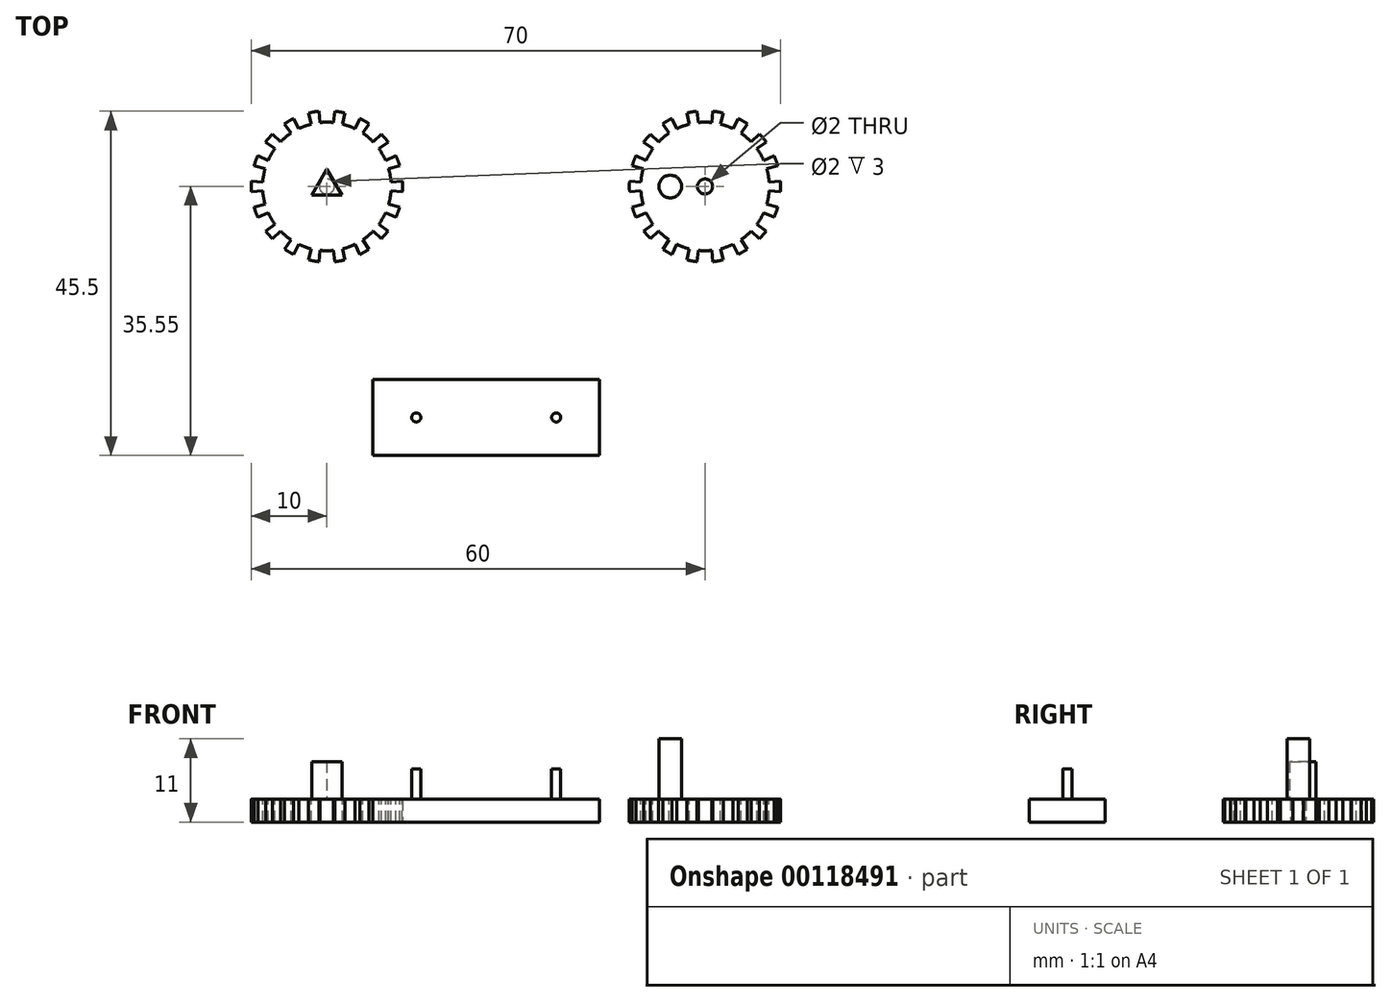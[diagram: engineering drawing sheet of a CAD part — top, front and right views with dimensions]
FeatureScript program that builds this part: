
annotation { "Feature Type Name" : "Feature", "Feature Type Description" : "" }
export const myFeature = defineFeature(function(context is Context, id is Id, definition is map)
    precondition{}
    {
        {
            var Q0;
            Q0=qCreatedBy(makeId("Top.planeOp"),FACE);
            var sketch = newSketch(context, id + "F0", { "sketchPlane" : qUnion([Q0])});
            skCircle(sketch, "E0", {"center": v(0, 0) * mm, "radius": 10 * mm});
            skSolve(sketch);
        }
        {
            var Q0;
            Q0=makeQuery(id+"F0.imprint","IMPRINT",FACE,{"disambiguationData":[TD([[makeQuery(id+"F0.imprint","IMPRINT",EDGE,{"derivedFrom":sQuery(id+"F0.wireOp",EDGE,"E0")}),1.0]])]});
            extrude(context, id + "F1", {"entities" : qUnion([Q0]), "depth" : 3 * mm});
        }
        {
            var Q0;
            Q0=makeQuery(id+"F1.opExtrude","CAP_FACE",FACE,{"disambiguationData":[OSD([sQuery(id+"F0.wireOp",EDGE,"E0")])],"isStart":false});
            var sketch = newSketch(context, id + "F2", { "sketchPlane" : qUnion([Q0])});
            skLineSegment(sketch, "E1", {"start": v(0, 10) * mm, "end": v(0, 8.5) * mm, "construction": true});
            skLineSegment(sketch, "E2", {"start": v(0.89, 8.45) * mm, "end": v(1.05, 9.95) * mm});
            skArc(sketch, "E3", {"start": v(0.89, 8.45) * mm, "mid": v(0, 8.5) * mm, "end": v(-0.89, 8.45) * mm});
            skLineSegment(sketch, "E4.MirrorCS", {"start": v(-0.89, 8.45) * mm, "end": v(-1.05, 9.95) * mm});
            skArc(sketch, "E5.0", {"start": v(1.05, 9.95) * mm, "mid": v(0, 10) * mm, "end": v(-1.05, 9.95) * mm});
            skSolve(sketch);
        }
        {
            var Q0;
            Q0=makeQuery(id+"F2.imprint","IMPRINT",FACE,{"disambiguationData":[TD([[makeQuery(id+"F2.imprint","IMPRINT",EDGE,{"derivedFrom":sQuery(id+"F2.wireOp",EDGE,"E2")}),1.0]])]});
            extrude(context, id + "F3", {"entities" : qUnion([Q0]), "operationType" : NewBodyOperationType.REMOVE, "endBound" : BoundingType.THROUGH_ALL, "oppositeDirection" : true, "depth" : 25 * mm});
        }
        {
            var Q0;
            Q0=makeQuery(id+"F1.opExtrude","SWEPT_BODY",BODY,{"disambiguationData":[OSD([sQuery(id+"F0.wireOp",EDGE,"E0")])]});
            var Q1;
            Q1=makeQuery(id+"F3.boolean.opBoolean","COPY",FACE,{"derivedFrom":makeQuery(id+"F3.opExtrude","SWEPT_FACE",FACE,{"disambiguationData":[OSD([sQuery(id+"F2.wireOp",EDGE,"E4.MirrorCS")])]})});
            var Q2;
            Q2=makeQuery(id+"F3.boolean.opBoolean","COPY",FACE,{"derivedFrom":makeQuery(id+"F3.opExtrude","SWEPT_FACE",FACE,{"disambiguationData":[OSD([sQuery(id+"F2.wireOp",EDGE,"E3")])]})});
            var Q3;
            Q3=makeQuery(id+"F3.boolean.opBoolean","COPY",FACE,{"derivedFrom":makeQuery(id+"F3.opExtrude","SWEPT_FACE",FACE,{"disambiguationData":[OSD([sQuery(id+"F2.wireOp",EDGE,"E2")])]})});
            var Q4;
            Q4=makeQuery(id+"F1.opExtrude","SWEPT_FACE",FACE,{"disambiguationData":[OSD([sQuery(id+"F0.wireOp",EDGE,"E0")])]});
            circularPattern(context, id + "F4", {"patternType" : PatternType.FACE, "faces" : qUnion([Q1, Q2, Q3]), "axis" : qUnion([Q4]), "angle" : 20 * degree, "instanceCount" : 18});
        }
        {
            var Q0;
            Q0=qCreatedBy(makeId("Right.planeOp"),FACE);
            cPlane(context, id + "F5", {"entities" : qUnion([Q0]), "cplaneType" : CPlaneType.OFFSET, "offset" : 25 * mm, "width" : 150 * mm, "height" : 150 * mm});
        }
        {
            var Q0;
            Q0=makeQuery(id+"F1.opExtrude","CAP_FACE",FACE,{"disambiguationData":[OSD([sQuery(id+"F0.wireOp",EDGE,"E0")])],"isStart":false});
            var sketch = newSketch(context, id + "F6", { "sketchPlane" : qUnion([Q0])});
            skCircle(sketch, "E6.cCircle", {"center": v(0, 0) * mm, "radius": 1.15 * mm, "construction": true});
            skLineSegment(sketch, "E6.0", {"start": v(0, 2.3) * mm, "end": v(2, -1.15) * mm});
            skLineSegment(sketch, "E6.1", {"start": v(2, -1.15) * mm, "end": v(-2, -1.15) * mm});
            skLineSegment(sketch, "E6.2", {"start": v(-2, -1.15) * mm, "end": v(0, 2.3) * mm});
            skPoint(sketch, "E6.0.midPoint", {"position": v(1, 0.58) * mm});
            skSolve(sketch);
        }
        {
            var Q0;
            Q0=makeQuery(id+"F1.opExtrude","CAP_FACE",FACE,{"disambiguationData":[OSD([sQuery(id+"F0.wireOp",EDGE,"E0")])],"isStart":true});
            var sketch = newSketch(context, id + "F7", { "sketchPlane" : qUnion([Q0])});
            skCircle(sketch, "E7", {"center": v(0, 0) * mm, "radius": 1 * mm});
            skSolve(sketch);
        }
        {
            var Q0;
            Q0=makeQuery(id+"F7.imprint","IMPRINT",FACE,{"disambiguationData":[TD([[makeQuery(id+"F7.imprint","IMPRINT",EDGE,{"derivedFrom":sQuery(id+"F7.wireOp",EDGE,"E7")}),1.0]])]});
            extrude(context, id + "F8", {"entities" : qUnion([Q0]), "operationType" : NewBodyOperationType.REMOVE, "oppositeDirection" : true, "depth" : 4 * mm});
        }
        {
            var Q0;
            Q0=makeQuery(id+"F1.opExtrude","SWEPT_BODY",BODY,{"disambiguationData":[OSD([sQuery(id+"F0.wireOp",EDGE,"E0")])]});
            var Q1;
            Q1=qCreatedBy(id+"F5.planeOp",FACE);
            mirror(context, id + "F9", {"entities" : qUnion([Q0]), "mirrorPlane" : qUnion([Q1])});
        }
        {
            var Q0;
            Q0 = qSketchRegion(id + "F6", true);
            extrude(context, id + "F10", {"entities" : qUnion([Q0]), "operationType" : NewBodyOperationType.ADD, "depth" : 5 * mm});
        }
        {
            var Q0;
            Q0=makeQuery(id+"F9.opPattern","COPY",FACE,{"derivedFrom":makeQuery(id+"F1.opExtrude","CAP_FACE",FACE,{"disambiguationData":[OSD([sQuery(id+"F0.wireOp",EDGE,"E0")])],"isStart":false}),"instanceName":"1"});
            var sketch = newSketch(context, id + "F11", { "sketchPlane" : qUnion([Q0])});
            skCircle(sketch, "E8", {"center": v(45.4, 0) * mm, "radius": 1.5 * mm});
            skSolve(sketch);
        }
        {
            var Q0;
            Q0=makeQuery(id+"F11.imprint","IMPRINT",FACE,{"disambiguationData":[TD([[makeQuery(id+"F11.imprint","IMPRINT",EDGE,{"derivedFrom":sQuery(id+"F11.wireOp",EDGE,"E8")}),1.0]])]});
            extrude(context, id + "F12", {"entities" : qUnion([Q0]), "operationType" : NewBodyOperationType.ADD, "depth" : 8 * mm});
        }
        {
            var Q0;
            Q0=qCreatedBy(makeId("Top.planeOp"),FACE);
            var sketch = newSketch(context, id + "F13", { "sketchPlane" : qUnion([Q0])});
            skLineSegment(sketch, "E9.bottom", {"start": v(6.07, -25.55) * mm, "end": v(36.07, -25.55) * mm});
            skLineSegment(sketch, "E9.top", {"start": v(6.07, -35.55) * mm, "end": v(36.07, -35.55) * mm});
            skLineSegment(sketch, "E9.left", {"start": v(6.07, -25.55) * mm, "end": v(6.07, -35.55) * mm});
            skLineSegment(sketch, "E9.right", {"start": v(36.07, -25.55) * mm, "end": v(36.07, -35.55) * mm});
            skSolve(sketch);
        }
        {
            var Q0;
            Q0=makeQuery(id+"F13.imprint","IMPRINT",FACE,{"disambiguationData":[TD([[makeQuery(id+"F13.imprint","IMPRINT",EDGE,{"derivedFrom":sQuery(id+"F13.wireOp",EDGE,"E9.bottom")}),-1.0]])]});
            extrude(context, id + "F14", {"entities" : qUnion([Q0]), "depth" : 3 * mm});
        }
        {
            var Q0;
            Q0=makeQuery(id+"F14.opExtrude","CAP_FACE",FACE,{"disambiguationData":[OSD([sQuery(id+"F13.wireOp",EDGE,"E9.bottom"),sQuery(id+"F13.wireOp",EDGE,"E9.top"),sQuery(id+"F13.wireOp",EDGE,"E9.left"),sQuery(id+"F13.wireOp",EDGE,"E9.right")])],"isStart":false});
            var sketch = newSketch(context, id + "F15", { "sketchPlane" : qUnion([Q0])});
            skCircle(sketch, "E10", {"center": v(11.82, -30.55) * mm, "radius": 0.6 * mm});
            skLineSegment(sketch, "E11", {"start": v(11.82, -30.55) * mm, "end": v(30.32, -30.55) * mm, "construction": true});
            skCircle(sketch, "E12", {"center": v(30.32, -30.55) * mm, "radius": 0.6 * mm});
            skLineSegment(sketch, "E13", {"start": v(21.07, -25.55) * mm, "end": v(21.07, -30.55) * mm, "construction": true});
            skLineSegment(sketch, "E14", {"start": v(21.07, -30.55) * mm, "end": v(21.07, -35.55) * mm, "construction": true});
            skSolve(sketch);
        }
        {
            var Q0;
            Q0 = qSketchRegion(id + "F15", true);
            extrude(context, id + "F16", {"entities" : qUnion([Q0]), "operationType" : NewBodyOperationType.ADD, "depth" : 4 * mm});
        }
    });
